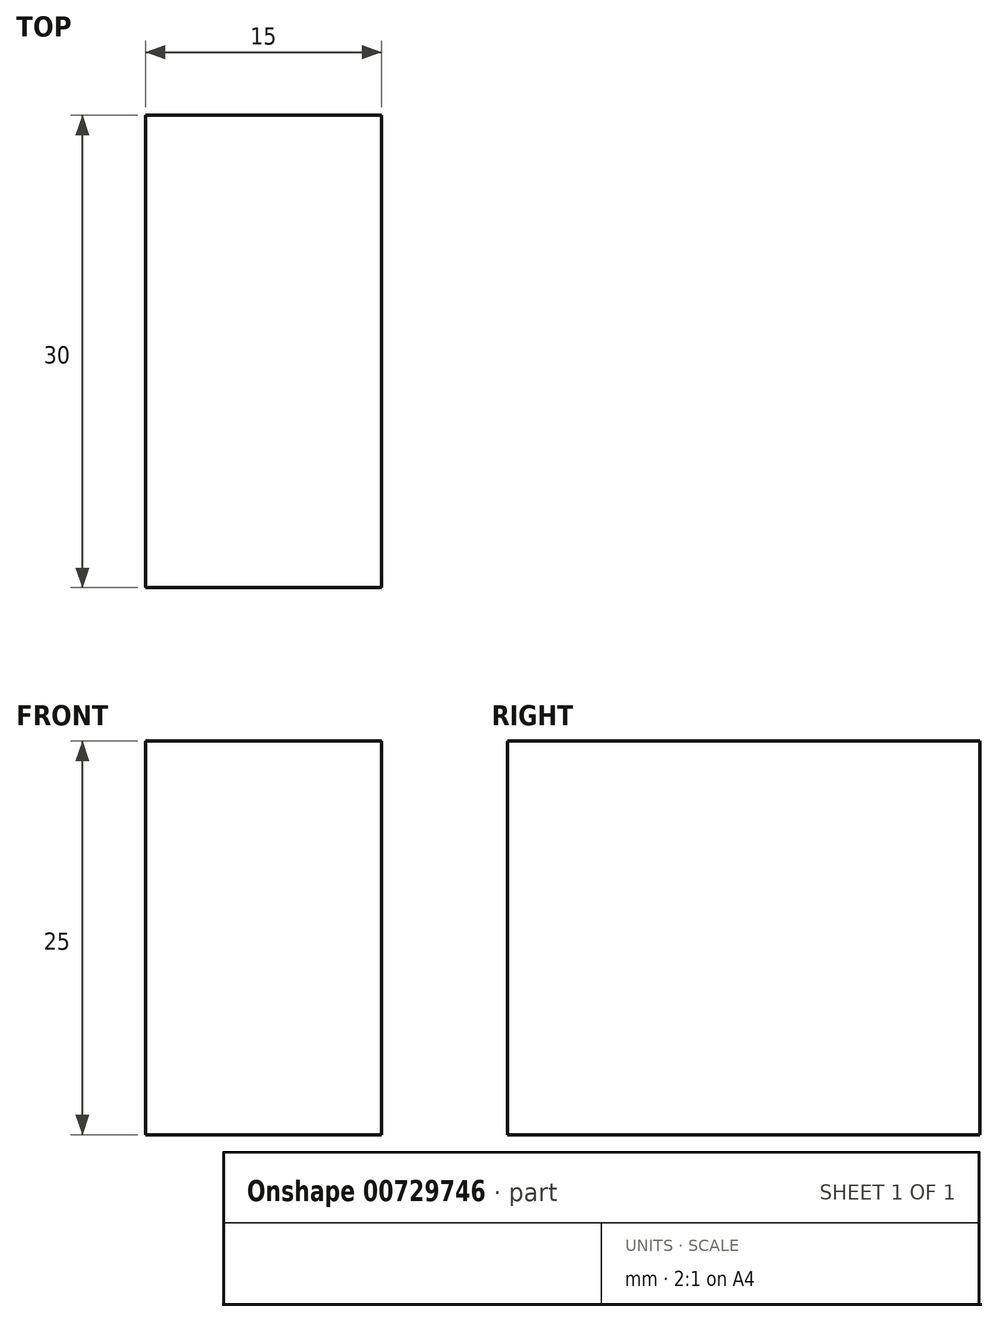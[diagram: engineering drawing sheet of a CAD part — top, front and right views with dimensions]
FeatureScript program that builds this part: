
annotation { "Feature Type Name" : "Feature", "Feature Type Description" : "" }
export const myFeature = defineFeature(function(context is Context, id is Id, definition is map)
    precondition{}
    {
        {
            var Q0;
            Q0=qCreatedBy(makeId("Top.planeOp"),FACE);
            var sketch = newSketch(context, id + "F0", { "sketchPlane" : qUnion([Q0])});
            skLineSegment(sketch, "E0.bottom", {"start": v(7.5, -15) * mm, "end": v(-7.5, -15) * mm});
            skLineSegment(sketch, "E0.top", {"start": v(7.5, 15) * mm, "end": v(-7.5, 15) * mm});
            skLineSegment(sketch, "E0.left", {"start": v(7.5, -15) * mm, "end": v(7.5, 15) * mm});
            skLineSegment(sketch, "E0.right", {"start": v(-7.5, -15) * mm, "end": v(-7.5, 15) * mm});
            skPoint(sketch, "E0.middle", {"position": v(0, 0) * mm});
            skSolve(sketch);
        }
        {
            var Q0;
            Q0 = qSketchRegion(id + "F0", true);
            extrude(context, id + "F1", {"entities" : qUnion([Q0]), "endBound" : BoundingType.SYMMETRIC, "depth" : 25 * mm, "offsetDistance" : 25 * mm});
        }
    });
